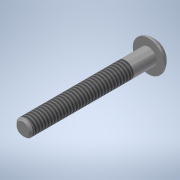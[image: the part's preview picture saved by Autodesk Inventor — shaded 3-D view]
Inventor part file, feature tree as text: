
AUTODESK INVENTOR PART (.ipt)
format: ipt  version: 2020 (Build 240168000, 168)  size: 155,648 bytes
history: native  units: in
note: dims shown in document units (in); Inventor stores cm internally (conversion verified against a paired STEP export)
features: sketch x3, extrude x2, revolve x1, chamfer x1, thread x1
ambient origin geometry x8: Origin, YZ Plane, XZ Plane, XY Plane, X Axis, Y Axis, Z Axis, Center Point
bodies: Solid1 (feature_tree)
feature tree (8):
  extrude  "Extrusion1"  Depth=1.25in TaperAngle=0.0deg
  revolve  "Revolution1"  [1 undecoded]
  extrude  "Extrusion2"  Depth=0.0938in
  chamfer  "Chamfer1"  Distance=0.0625in
  thread  "Thread1"  [1 undecoded]
  sketch  "Sketch1"  dims[d0=0.164in d1=1.25in d2=0.0in]
  sketch  "Sketch2"  dims[d3=0.087in d6=0.08in]
  sketch  "Sketch3"  dims[d7=90.0deg d8=0.0938in d9=0.0625in d10=0.0in d13=0.02in d14=0.125in d15=45.0deg d16=1.0in d17=0.0in d19=0.156in]
note: 2 required parameter values undecoded (feature->parameter linkage not recoverable at this tier; creation-order binding heuristic only, values carry confidence <= 0.55)